# Revit family: Hand_Dryer-Excel_Dryer-Wall_Guard
name_source: partatom
category: Specialty Equipment
revit_build: Autodesk Revit 2015 (Build: 20140606_1530(x64)
units: mm (PartAtom-declared; Revit-internal decimal feet)

## types (3) — shared parameters
Default Elevation = 1' - 5 9/16"
Depth = 0' - 0 1/16"
Description = Wall Guard
Height = 2' - 8"
Manufacturer = Excel Dryer
Product Documentation Link = http://www.exceldryer.com
Product Name = XLERATOR Wall Guard
Product Page URL = http://www.exceldryer.com
URL = http://www.exceldryer.com
Width = 1' - 4"

## per-type parameters (varying)
| type | Model | Product data url | Wall Guard Material |
| 89S | Wall Guard Stainless | https://bimobject.com | Metal - Excel Dryer - Stainless Steel - Brushed |
| 89B | Wall Guard Black | hhttps://bimobject.com | Plastic - Excel Dryer - Anti-Microbial - Black |
| 89W | Wall Guard White | https://bimobject.com | Plastic - Excel Dryer - Anti-Microbial - White |

## geometry (parser evidence)
native form markers: Sweep x3
no freeform markers — native parametric forms only
